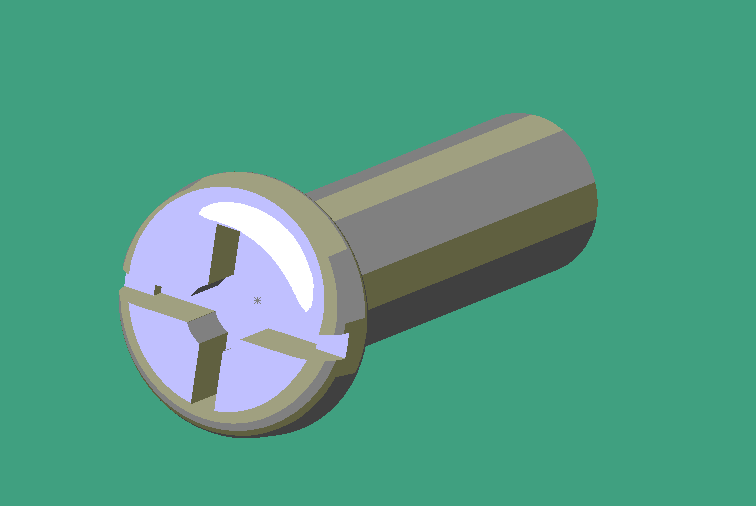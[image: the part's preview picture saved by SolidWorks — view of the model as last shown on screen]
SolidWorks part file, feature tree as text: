
SOLIDWORKS PART (.sldprt)
format: sldprt  version: not decoded by parser v0  size: 185,344 bytes
history: native  units: mm
features: sketch x4, plane x3, extrude x2, fillet x2, cut_extrude x2, material x1, chamfer x1 (+8 scaffold rows collapsed)
feature tree (23):
  scaffold x8  (default folders/planes/origin — collapsed)
  material  "Matériau <non spécifié>"
  plane  "Plane1"
  plane  "Plane2"
  plane  "Plane3"
  sketch  "Esquisse1"  dims[D1=5.0mm]
  extrude  "Base-Extrusion"  Depth=1.5mm
  fillet  "Congé1"  Radius=0.75mm
  fillet  "Congé2"  Radius=0.25mm
  sketch  "Esquisse2"  dims[D1=3.0mm]
  extrude  "Boss.-Extru.1"  Depth=10mm
  chamfer  "Chanfrein1"  Distance=0.5mm Angle=45deg
  sketch  "Esquisse4"  dims[D1=1.25mm D2=0.5mm D3=1.75mm D4=~1.100481mm]
  cut_extrude  "Enlèv. mat.-Extru.1"  Depth=1mm
  sketch  "Esquisse5"
  cut_extrude  "Enlèv. mat.-Extru.2"  Depth=0.75mm
decode coverage: 10 of 11 modeling features carry decoded parameters
note: ~ marks probable driven/reference dimensions
note: suppression state not decoded; provenance and decode notes live in map.json
